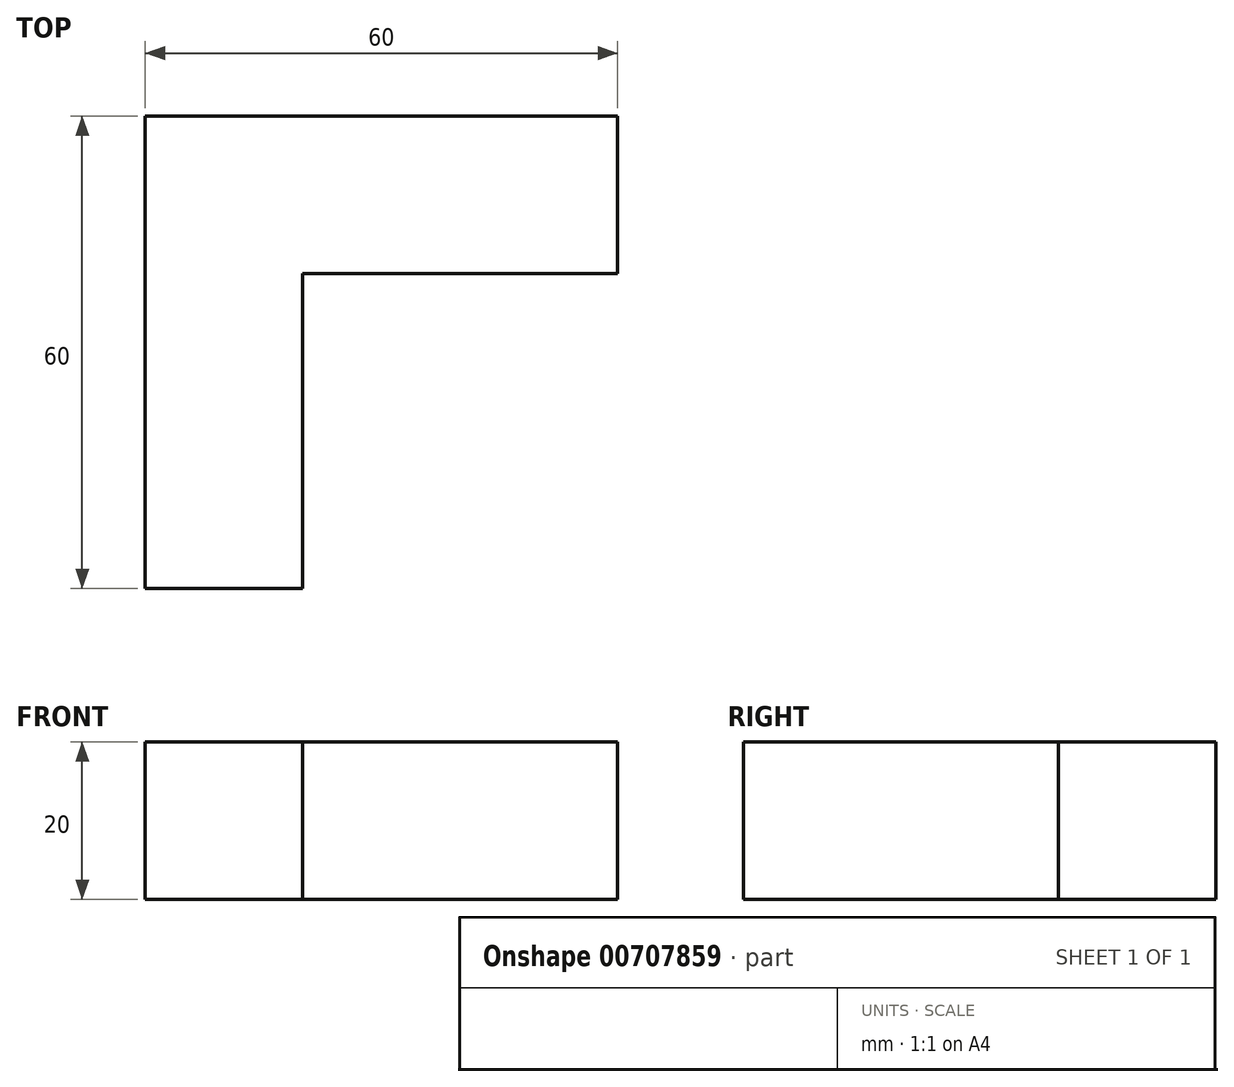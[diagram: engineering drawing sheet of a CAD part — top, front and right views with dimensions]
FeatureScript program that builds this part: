
annotation { "Feature Type Name" : "Feature", "Feature Type Description" : "" }
export const myFeature = defineFeature(function(context is Context, id is Id, definition is map)
    precondition{}
    {
        {
            var Q0;
            Q0=qCreatedBy(makeId("Top.planeOp"),FACE);
            var sketch = newSketch(context, id + "F0", { "sketchPlane" : qUnion([Q0])});
            skLineSegment(sketch, "E0", {"start": v(-40.52, -55.07) * mm, "end": v(-40.52, -15.07) * mm});
            skLineSegment(sketch, "E1", {"start": v(-40.52, -15.07) * mm, "end": v(-0.52, -15.07) * mm});
            skLineSegment(sketch, "E2.0", {"start": v(-60.52, 4.93) * mm, "end": v(-0.52, 4.93) * mm});
            skLineSegment(sketch, "E3.1", {"start": v(-60.52, -55.07) * mm, "end": v(-60.52, 4.93) * mm});
            skLineSegment(sketch, "E4", {"start": v(-60.52, -55.07) * mm, "end": v(-40.52, -55.07) * mm});
            skLineSegment(sketch, "E5", {"start": v(-0.52, -15.07) * mm, "end": v(-0.52, 4.93) * mm});
            skSolve(sketch);
        }
        {
            var Q0;
            Q0 = qSketchRegion(id + "F0", true);
            extrude(context, id + "F1", {"entities" : qUnion([Q0]), "depth" : 20 * mm, "offsetDistance" : 25 * mm});
        }
    });
